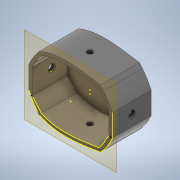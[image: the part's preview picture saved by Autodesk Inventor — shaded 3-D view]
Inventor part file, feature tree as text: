
AUTODESK INVENTOR PART (.ipt)
format: ipt  version: 2021.1 (Build 251245010, 245A)  size: 239,616 bytes
history: native  units: mm
features: sketch x4, extrude x4, plane x4, mirror x1
ambient origin geometry x8: Origin, YZ Plane, XZ Plane, XY Plane, X Axis, Y Axis, Z Axis, Center Point
bodies: Solid1 (feature_tree)
feature tree (13):
  sketch  "Sketch1"  dims[d1=70.0mm d2=70.0mm]
  sketch  "Sketch2"  dims[d3=0.0mm d4=6.0mm]
  extrude  "Extrusion1"  Depth=70.0mm
  extrude  "Extrusion2"  Depth=6.0mm
  plane  "Work Plane1"
  extrude  "Extrusion3"  TaperAngle=0.0deg  [1 undecoded]
  plane  "Work Plane2"
  sketch  "Sketch5"  dims[d5=64.0mm d6=0.0mm]
  mirror  "Mirror1"
  plane  "Work Plane3"
  extrude  "Extrusion4"  Depth=6.0mm TaperAngle=0.0deg
  plane  "Work Plane4"
  sketch  "Sketch6"  dims[d7=60.0mm d9=300.0mm d10=0.0mm d11=49.151954mm d12=49.152mm d13=10.0mm d14=10.0mm d15=20.0mm d16=0.0mm d19=40.0mm d20=6.0mm d21=6.0mm d22=35.0mm]
note: 1 required parameter value undecoded (feature->parameter linkage not recoverable at this tier; creation-order binding heuristic only, values carry confidence <= 0.55)
